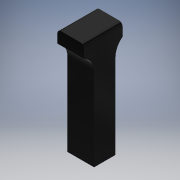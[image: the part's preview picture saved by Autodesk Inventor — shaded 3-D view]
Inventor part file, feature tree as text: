
AUTODESK INVENTOR PART (.ipt)
format: ipt  version: 2019 (Build 230136000, 136)  size: 138,240 bytes
history: native  units: mm
features: extrude x3, sketch x3, fillet x2
ambient origin geometry x8: Origin, YZ Plane, XZ Plane, XY Plane, X Axis, Y Axis, Z Axis, Center Point
bodies: Solid1 (feature_tree)
feature tree (8):
  extrude  "Extrusion1"  Depth=15.0mm
  extrude  "Extrusion2"  Depth=7.5mm
  fillet  "Fillet2"  Radius=3.5mm
  extrude  "Extrusion3"  Depth=16.0mm TaperAngle=0.0deg
  fillet  "Fillet3"  Radius=4.0mm
  sketch  "Sketch1"  dims[d0=4.0mm d1=15.0mm]
  sketch  "Sketch2"  dims[d2=7.0mm d3=7.5mm d4=3.5mm]
  sketch  "Sketch4"  dims[d5=2.0mm d6=16.0mm d7=0.0mm d8=4.0mm d9=0.0mm d10=55.5mm d11=0.0mm d13=10.0mm d14=2.0mm d15=5.6mm d16=0.0mm d17=10.0mm d18=15.0mm d19=12.0mm]
